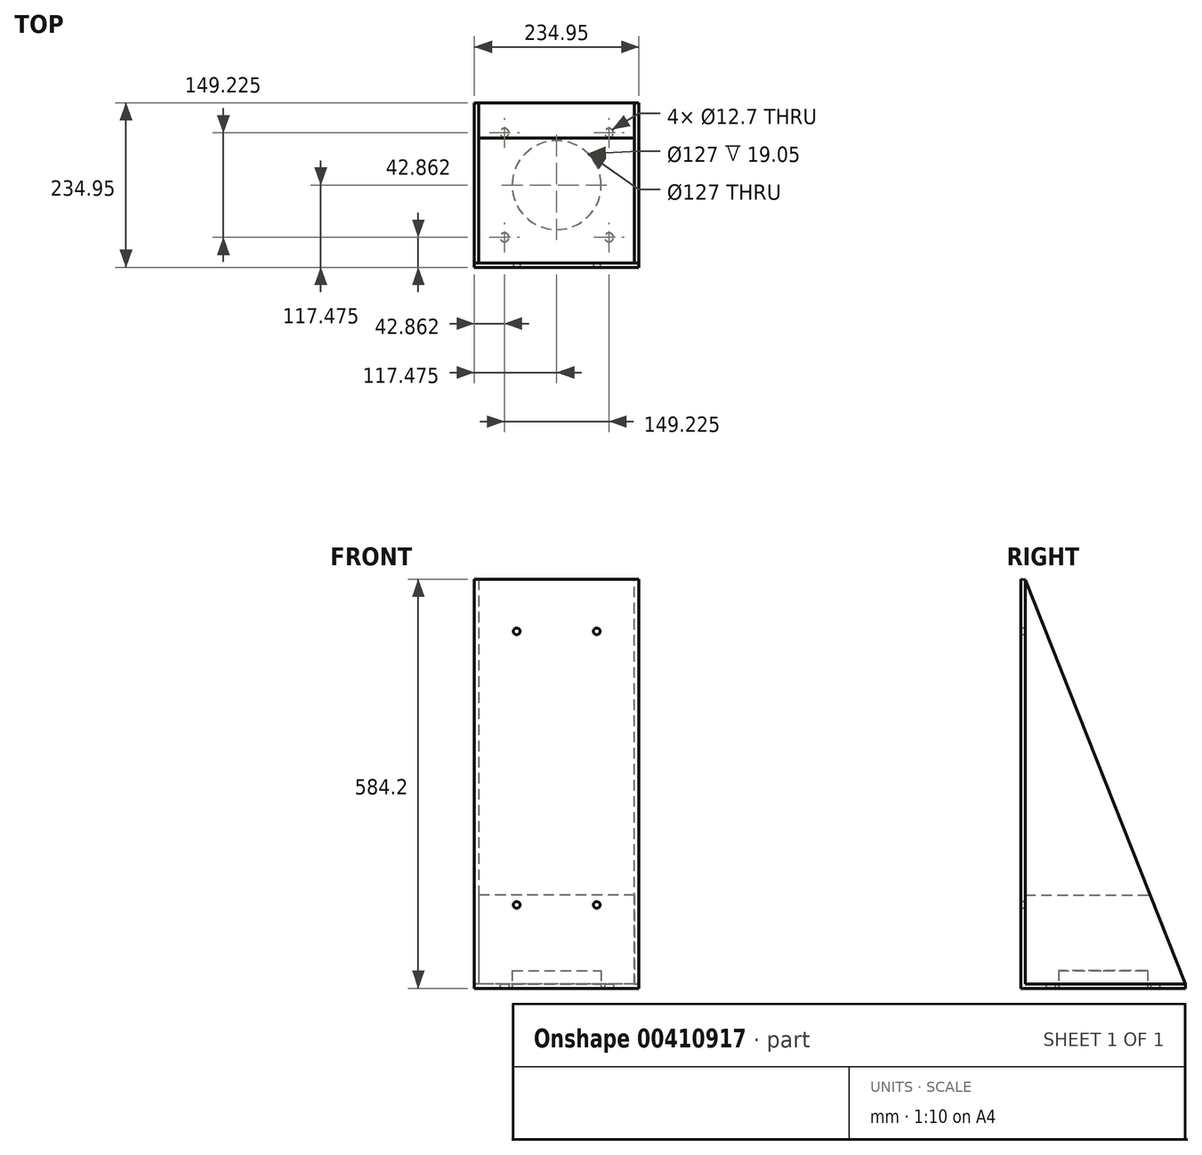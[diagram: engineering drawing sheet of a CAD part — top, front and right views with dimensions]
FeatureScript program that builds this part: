
annotation { "Feature Type Name" : "Feature", "Feature Type Description" : "" }
export const myFeature = defineFeature(function(context is Context, id is Id, definition is map)
    precondition{}
    {
        {
            var Q0;
            Q0=qCreatedBy(makeId("Top.planeOp"),FACE);
            var sketch = newSketch(context, id + "F0", { "sketchPlane" : qUnion([Q0])});
            skLineSegment(sketch, "E0", {"start": v(0, 0) * mm, "end": v(-234.95, 0) * mm});
            skLineSegment(sketch, "E1", {"start": v(-234.95, 0) * mm, "end": v(-234.95, 234.95) * mm});
            skLineSegment(sketch, "E2", {"start": v(-234.95, 234.95) * mm, "end": v(0, 234.95) * mm});
            skLineSegment(sketch, "E3", {"start": v(0, 234.95) * mm, "end": v(0, 0) * mm});
            skSolve(sketch);
        }
        {
            var Q0;
            Q0=qSketchRegion(id+"F0",true);
            extrude(context, id + "F1", {"entities" : qUnion([Q0]), "depth" : 584.2 * mm});
        }
        {
            var Q0;
            Q0=makeQuery(id+"F1.opExtrude","SWEPT_FACE",FACE,{"disambiguationData":[OSD([sQuery(id+"F0.wireOp",EDGE,"E3")])]});
            var sketch = newSketch(context, id + "F2", { "sketchPlane" : qUnion([Q0])});
            skLineSegment(sketch, "E4", {"start": v(234.95, 558.8) * mm, "end": v(0, 584.2) * mm});
            skLineSegment(sketch, "E5", {"start": v(234.95, 558.8) * mm, "end": v(234.95, 584.2) * mm});
            skLineSegment(sketch, "E6", {"start": v(234.95, 584.2) * mm, "end": v(0, 584.2) * mm});
            skSolve(sketch);
        }
        {
            var Q0;
            Q0=makeQuery(id+"F2.imprint","IMPRINT",FACE,{"disambiguationData":[TD([[makeQuery(id+"F2.imprint","IMPRINT",EDGE,{"derivedFrom":sQuery(id+"F2.wireOp",EDGE,"E4")}),-1.0]])]});
            extrude(context, id + "F3", {"entities" : qUnion([Q0]), "operationType" : NewBodyOperationType.REMOVE, "endBound" : BoundingType.THROUGH_ALL, "oppositeDirection" : true, "depth" : 25.4 * mm});
        }
        {
            var Q0;
            {var subQ0=sQuery(id+"F0.wireOp",EDGE,"E0");Q0=makeQuery(id+"FEAy7TYS6UcWf4X_1.boolean.opBoolean","MERGE",FACE,{"derivedFrom":[makeQuery(id+"F1.opExtrude","SWEPT_FACE",FACE,{"disambiguationData":[OSD([subQ0])]}),makeQuery(id+"FEAy7TYS6UcWf4X_1.opExtrude","SWEPT_FACE",FACE,{"disambiguationData":[OSD([subQ0])]})]});}
            var sketch = newSketch(context, id + "F4", { "sketchPlane" : qUnion([Q0])});
            skLineSegment(sketch, "E7", {"start": v(-117.48, 0) * mm, "end": v(-117.48, 509.59) * mm});
            skPoint(sketch, "E8.endSnap0", {"position": v(-117.47, 584.2) * mm});
            skLineSegment(sketch, "E9", {"start": v(-117.48, 509.59) * mm, "end": v(-60.33, 509.59) * mm});
            skLineSegment(sketch, "E10", {"start": v(-117.48, 509.59) * mm, "end": v(-174.63, 509.59) * mm});
            skCircle(sketch, "E11", {"center": v(-60.33, 509.59) * mm, "radius": 4.76 * mm});
            skCircle(sketch, "E12", {"center": v(-174.63, 509.59) * mm, "radius": 4.76 * mm});
            skLineSegment(sketch, "E13", {"start": v(-174.63, 509.59) * mm, "end": v(-174.62, 119.06) * mm});
            skLineSegment(sketch, "E14", {"start": v(-60.33, 509.59) * mm, "end": v(-60.33, 119.06) * mm});
            skCircle(sketch, "E15", {"center": v(-174.62, 119.06) * mm, "radius": 4.76 * mm});
            skCircle(sketch, "E16", {"center": v(-60.33, 119.06) * mm, "radius": 4.76 * mm});
            skSolve(sketch);
        }
        {
            var Q0;
            Q0=qSketchRegion(id+"F4",true);
            extrude(context, id + "F5", {"entities" : qUnion([Q0]), "operationType" : NewBodyOperationType.REMOVE, "oppositeDirection" : true, "depth" : 25.4 * mm});
        }
        {
            var Q0;
            Q0=qSketchRegion(id+"F4",true);
            extrude(context, id + "F6", {"entities" : qUnion([Q0]), "operationType" : NewBodyOperationType.REMOVE, "oppositeDirection" : true, "depth" : 25.4 * mm});
        }
        {
            var Q0;
            Q0=makeQuery(id+"F1.opExtrude","SWEPT_FACE",FACE,{"disambiguationData":[OSD([sQuery(id+"F0.wireOp",EDGE,"E3")])]});
            var sketch = newSketch(context, id + "F7", { "sketchPlane" : qUnion([Q0])});
            skLineSegment(sketch, "E17", {"start": v(0, 0) * mm, "end": v(6.35, 0) * mm});
            skLineSegment(sketch, "E18", {"start": v(6.35, 0) * mm, "end": v(6.35, 6.35) * mm});
            skLineSegment(sketch, "E19.bottom", {"start": v(6.35, 6.35) * mm, "end": v(445.92, 6.35) * mm});
            skLineSegment(sketch, "E19.top", {"start": v(6.35, 612) * mm, "end": v(445.92, 612) * mm});
            skLineSegment(sketch, "E19.left", {"start": v(6.35, 6.35) * mm, "end": v(6.35, 612) * mm});
            skLineSegment(sketch, "E19.right", {"start": v(445.92, 6.35) * mm, "end": v(445.92, 612) * mm});
            skSolve(sketch);
        }
        {
            var Q0;
            Q0=qSketchRegion(id+"F7",true);
            extrude(context, id + "F8", {"entities" : qUnion([Q0]), "operationType" : NewBodyOperationType.REMOVE, "endBound" : BoundingType.THROUGH_ALL, "oppositeDirection" : true, "depth" : 25.4 * mm});
        }
        {
            var Q0;
            Q0=makeQuery(id+"F1.opExtrude","SWEPT_FACE",FACE,{"disambiguationData":[OSD([sQuery(id+"F0.wireOp",EDGE,"E3")])]});
            var sketch = newSketch(context, id + "F9", { "sketchPlane" : qUnion([Q0])});
            skLineSegment(sketch, "E20", {"start": v(6.35, 583.51) * mm, "end": v(6.35, 6.35) * mm});
            skLineSegment(sketch, "E21", {"start": v(6.35, 6.35) * mm, "end": v(234.95, 6.35) * mm});
            skLineSegment(sketch, "E22", {"start": v(234.95, 6.35) * mm, "end": v(6.35, 583.51) * mm});
            skSolve(sketch);
        }
        {
            var Q0;
            Q0=qSketchRegion(id+"F9",true);
            extrude(context, id + "F10", {"entities" : qUnion([Q0]), "oppositeDirection" : true, "depth" : 6.35 * mm});
        }
        {
            var Q0;
            Q0=makeQuery(id+"F1.opExtrude","SWEPT_FACE",FACE,{"disambiguationData":[OSD([sQuery(id+"F0.wireOp",EDGE,"E1")])]});
            var sketch = newSketch(context, id + "F11", { "sketchPlane" : qUnion([Q0])});
            skLineSegment(sketch, "E23", {"start": v(-6.35, 583.51) * mm, "end": v(-6.35, 6.35) * mm});
            skLineSegment(sketch, "E24", {"start": v(-6.35, 6.35) * mm, "end": v(-234.95, 6.35) * mm});
            skLineSegment(sketch, "E25", {"start": v(-234.95, 6.35) * mm, "end": v(-6.35, 583.51) * mm});
            skSolve(sketch);
        }
        {
            var Q0;
            Q0=qSketchRegion(id+"F11",true);
            extrude(context, id + "F12", {"entities" : qUnion([Q0]), "operationType" : NewBodyOperationType.ADD, "oppositeDirection" : true, "depth" : 6.35 * mm});
        }
        {
            var Q0;
            Q0=makeQuery(id+"F1.opExtrude","CAP_FACE",FACE,{"disambiguationData":[OSD([sQuery(id+"F0.wireOp",EDGE,"E0"),sQuery(id+"F0.wireOp",EDGE,"E1"),sQuery(id+"F0.wireOp",EDGE,"E2"),sQuery(id+"F0.wireOp",EDGE,"E3")])],"isStart":true});
            var sketch = newSketch(context, id + "F13", { "sketchPlane" : qUnion([Q0])});
            skCircle(sketch, "E26", {"center": v(-192.09, -42.86) * mm, "radius": 6.35 * mm});
            skCircle(sketch, "E27", {"center": v(-42.86, -42.86) * mm, "radius": 6.35 * mm});
            skCircle(sketch, "E28", {"center": v(-42.86, -192.09) * mm, "radius": 6.35 * mm});
            skCircle(sketch, "E29", {"center": v(-192.09, -192.09) * mm, "radius": 6.35 * mm});
            skSolve(sketch);
        }
        {
            var Q0;
            Q0=qSketchRegion(id+"F13",true);
            extrude(context, id + "F14", {"entities" : qUnion([Q0]), "operationType" : NewBodyOperationType.REMOVE, "endBound" : BoundingType.THROUGH_ALL, "oppositeDirection" : true, "depth" : 25.4 * mm});
        }
        {
            var Q0;
            Q0=makeQuery(id+"F12.opExtrude","CAP_FACE",FACE,{"disambiguationData":[OSD([sQuery(id+"F11.wireOp",EDGE,"E23"),sQuery(id+"F11.wireOp",EDGE,"E24"),sQuery(id+"F11.wireOp",EDGE,"E25")])],"isStart":false});
            var sketch = newSketch(context, id + "F15", { "sketchPlane" : qUnion([Q0])});
            skLineSegment(sketch, "E30", {"start": v(234.95, 6.35) * mm, "end": v(6.35, 6.35) * mm});
            skLineSegment(sketch, "E31", {"start": v(6.35, 6.35) * mm, "end": v(6.35, 133.35) * mm});
            skLineSegment(sketch, "E32", {"start": v(6.35, 133.35) * mm, "end": v(184.65, 133.35) * mm});
            skLineSegment(sketch, "E33", {"start": v(184.65, 133.35) * mm, "end": v(234.95, 6.35) * mm});
            skSolve(sketch);
        }
        {
            var Q0;
            Q0 = qSketchRegion(id + "F15", true);
            var Q1;
            Q1=makeQuery(id+"F10.opExtrude","CAP_FACE",FACE,{"disambiguationData":[OSD([sQuery(id+"F9.wireOp",EDGE,"E20"),sQuery(id+"F9.wireOp",EDGE,"E21"),sQuery(id+"F9.wireOp",EDGE,"E22")])],"isStart":false});
            extrude(context, id + "F16", {"entities" : qUnion([Q0]), "endBound" : BoundingType.UP_TO_SURFACE, "endBoundEntityFace" : qUnion([Q1]), "depth" : 25.4 * mm});
        }
        {
            var Q0;
            Q0=makeQuery(id+"F1.opExtrude","CAP_FACE",FACE,{"disambiguationData":[OSD([sQuery(id+"F0.wireOp",EDGE,"E0"),sQuery(id+"F0.wireOp",EDGE,"E1"),sQuery(id+"F0.wireOp",EDGE,"E2"),sQuery(id+"F0.wireOp",EDGE,"E3")])],"isStart":true});
            var sketch = newSketch(context, id + "F17", { "sketchPlane" : qUnion([Q0])});
            skCircle(sketch, "E34", {"center": v(-117.48, -117.48) * mm, "radius": 63.5 * mm});
            skSolve(sketch);
        }
        {
            var Q0;
            Q0 = qSketchRegion(id + "F17", true);
            extrude(context, id + "F18", {"entities" : qUnion([Q0]), "operationType" : NewBodyOperationType.REMOVE, "oppositeDirection" : true, "depth" : 25.4 * mm});
        }
    });
